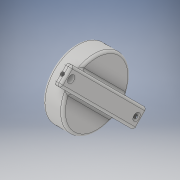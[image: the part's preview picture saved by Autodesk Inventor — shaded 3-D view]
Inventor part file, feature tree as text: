
AUTODESK INVENTOR PART (.ipt)
format: ipt  version: 2019 (Build 230136000, 136)  size: 401,408 bytes
history: native  units: in
note: dims shown in document units (in); Inventor stores cm internally (conversion verified against a paired STEP export)
features: sketch x13, extrude x11, plane x4, mirror x3, thread x2, fillet x2, pattern_circular x1, projected_geometry x1
ambient origin geometry x8: Origin, YZ Plane, XZ Plane, XY Plane, X Axis, Y Axis, Z Axis, Center Point
bodies: Solid1 (feature_tree), Solid2 (feature_tree)
feature tree (37):
  extrude  "Extrusion1"  Depth=1.7323in
  extrude  "Extrusion3"  Depth=1.2402in
  extrude  "Extrusion4"  Depth=1.1811in TaperAngle=0.0deg
  pattern_circular  "Circular Pattern1"  Count=4 Angle=360.0deg
  sketch  "Sketch6"  dims[d16=0.3937in d17=45.0deg]
  plane  "Work Plane1"
  extrude  "Extrusion5"  TaperAngle=45.0deg  [1 undecoded]
  plane  "Work Plane2"
  mirror  "Mirror1"
  extrude  "Extrusion6"  TaperAngle=45.0deg  [1 undecoded]
  extrude  "Extrusion7"  Depth=0.2362in TaperAngle=0.0deg
  sketch  "Sketch11"  dims[d26=0.3937in d27=0.0in d28=0.0118in]
  plane  "Work Plane3"
  extrude  "Extrusion8"  TaperAngle=45.0deg  [1 undecoded]
  thread  "Thread1"  [1 undecoded]
  mirror  "Mirror2"
  extrude  "Extrusion9"  Depth=0.3937in
  extrude  "Extrusion14"  Depth=0.2362in
  extrude  "Extrusion15"  Depth=0.0098in
  extrude  "Extrusion16"  Depth=0.3937in
  thread  "Thread3"  [1 undecoded]
  plane  "Work Plane5"
  mirror  "Mirror3"
  fillet  "Fillet3"  Radius=0.3937in
  fillet  "Fillet4"  Radius=0.3937in
  sketch  "Sketch2"  dims[d3=0.7874in d4=1.7323in]
  sketch  "Sketch4"  dims[d5=0.4724in d6=0.0in d9=1.2402in]
  sketch  "Sketch5"  dims[d10=0.2008in d11=1.1811in d12=0.0in d13=1.5748in d14=360.0deg]
  sketch  "Sketch7"  dims[d18=0.1181in d19=45.0deg]
  sketch  "Sketch8"  dims[d20=0.3543in d21=0.2362in d22=0.0in]
  projected_geometry  "Projected Loop1"
  sketch  "Sketch9"  dims[d23=0.8661in d24=45.0deg d25=0.2047in]
  sketch  "Sketch12"  dims[d29=0.4724in d30=0.0in d31=0.2362in]
  sketch  "Sketch13"  dims[d32=0.4724in d33=0.0in d34=0.0098in]
  sketch  "Sketch22"  dims[d35=45.0deg d36=0.4724in d37=0.1969in d38=0.3937in d39=0.0in d40=0.3937in d41=0.0in]
  sketch  "Sketch23"  dims[d42=0.1969in d43=0.0in]
  sketch  "Sketch24"  dims[d73=3.5039in d74=225.0deg d75=0.5906in d76=0.2362in d77=0.0in d78=0.2362in d79=45.0deg d80=0.2402in d81=0.2047in d82=0.0in d83=0.1181in d84=0.2047in d85=0.0in d86=0.3937in d87=0.0in d88=0.0787in d89=0.0787in]
note: 5 required parameter values undecoded (feature->parameter linkage not recoverable at this tier; creation-order binding heuristic only, values carry confidence <= 0.55)
